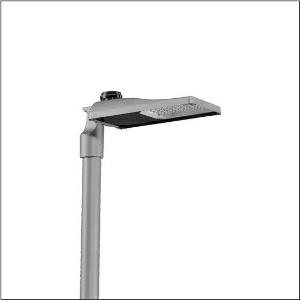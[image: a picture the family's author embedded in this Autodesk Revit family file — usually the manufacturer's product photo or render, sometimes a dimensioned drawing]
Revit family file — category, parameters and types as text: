
# Revit family: streetlight_sl_31_mini___st1_0a_5xh6d35n08ga_9230
name_source: partatom
category: Lighting Fixtures
units: mm (PartAtom-declared; Revit-internal decimal feet)

## family parameters
Cut with Voids When Loaded = No
Host = Face
Light Source = No
Part Type = Normal
Room Calculation Point = No
Round Connector Dimension = Use Diameter
Shared = No

## types (1)
- --- (1 x LED, 5710 lm, 37.3 W, 3000K)
    Apparent Load = 37 VA
    CIE Flux Codes = 37 72 97 100 100
    Color Rendering = 70
    Color Temperature = 3000K
    Default Elevation = 1800 mm
    Description = Streetlight SL 31 mini NEMA (7pin), Desk-Remote mast luminaire for post-top, side-entry; light control with lens of PMMA; light distribution: ST1.0a, direct asymmetric distribution, for standard-compliant lighting for roads and squares; LED: luminous flux: 5.710lm, light colour: 730, colour temperature: 3000K; luminous efficacy: 153,1lm/W; control: pre-setting: linear dimming characteristic, flexible luminous flux parameterisation, time-dependent luminous flux control, constant luminous flux control, intelligent temperature release in ECG and LED module, overheat protection; luminaire housing, of diecast aluminium, SITECO metallic grey (DB 702S), corrosivity category C5 high according to DIN EN ISO 12944; cover of toughened safety glass, transparent, opened without tools; mast flange of diecast aluminium, SITECO metallic grey (DB 702S), spigot size: 76/60mm, mast flange included unmounted; cable length: 6,5m, connection cable pre-assembled; mains connection: 220..240V, AC, 50/60Hz; power consumption (at start of service life): 37,3W / (at end of service life): 38,7W / (with reduced operation 50%): 17,5W; protection rating (complete): IP66; insulation class (complete): insulation class I (protective earthing); impact resistance: IK10; certification: CE, ENEC, ENEC+, VDE, UKCA; permissible operating ambient temperature for outdoor applications: -40..+50°C; packaging unit: 1 piece

Light Distribution: ST1.0a
    Height = 76 mm
    Lamp = 1 x LED
    Lamp Light Flux = 5710 lm
    Lamp Power = 37.3 W
    Lamp count = 1
    Length = 547 mm
    Luminous efficacy = 153 lm/W
    Manufacturer = Siteco
    ModVariant = No
    Model = 5XH6D35N08GA
    Number of Poles = 1
    OnlyDefault = Yes
    Power Factor = 1
    Product Name = Streetlight SL 31 mini | ST1.0a
    Product group = mast luminaire | pylon top
    ProductGroupID = 6100
    Protection Class = Protection class I
    Protection Degree = IP 66
    RLX_Detail_Level = 1
    RLX_Emergency_Light_Flux = 0 lm
    RLX_Emergency_Type = 0
    RLX_Emergency_Type_DB = No
    RlxData = <blob elided: 40313 chars, md5=b6ca4677>
    Socket = socket
    Standby Power = 0 W
    System Light Flux = 5710 lm
    System Power = 37 W
    Type Comments = factory setting: luminous flux: 100 % | dim-lin: 254 | 386 mA
    Type Image = l_1300322.jpg
    URL = http://relux.com
    VarID = @adj_060545
    Voltage = 0 V
    Weight = 0.00 kg
    Width = 265 mm

## geometry (parser evidence)
native form markers: Blend x4, Sweep x10
no freeform markers — native parametric forms only
